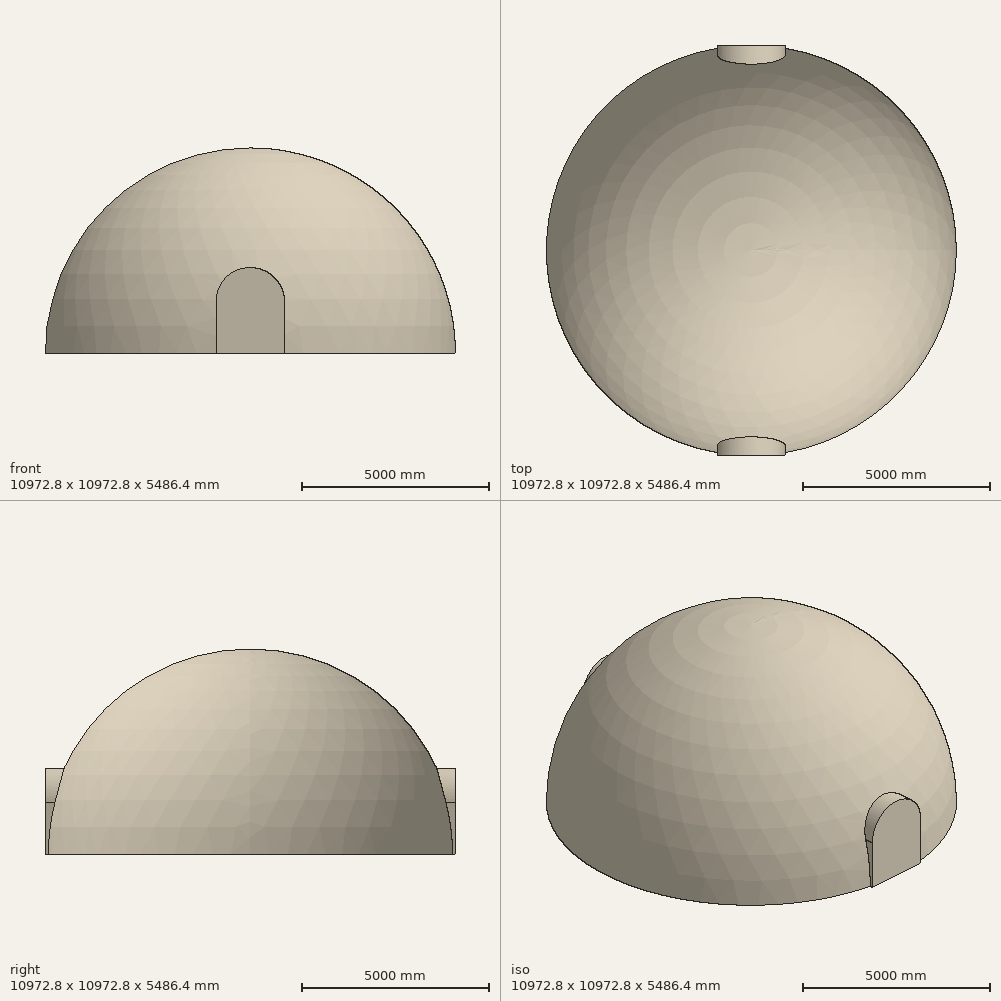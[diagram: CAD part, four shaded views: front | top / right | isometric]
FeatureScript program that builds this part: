
annotation { "Feature Type Name" : "Feature", "Feature Type Description" : "" }
export const myFeature = defineFeature(function(context is Context, id is Id, definition is map)
    precondition{}
    {
        {
            var Q0;
            Q0=qCreatedBy(makeId("Front.planeOp"),FACE);
            var sketch = newSketch(context, id + "F0", { "sketchPlane" : qUnion([Q0])});
            skLineSegment(sketch, "E0", {"start": v(0, 0) * mm, "end": v(5486.4, 0) * mm});
            skLineSegment(sketch, "E1", {"start": v(0, 0) * mm, "end": v(0, 5486.4) * mm, "construction": true});
            skArc(sketch, "E2", {"start": v(0, 5486.4) * mm, "mid": v(3879.47, 3879.47) * mm, "end": v(5486.4, 0) * mm});
            skLineSegment(sketch, "E3", {"start": v(0, 5486.4) * mm, "end": v(0, 0) * mm});
            skSolve(sketch);
        }
        {
            var Q0;
            Q0=makeQuery(id+"F0.imprint","IMPRINT",FACE,{"disambiguationData":[TD([[makeQuery(id+"F0.imprint","IMPRINT",EDGE,{"derivedFrom":sQuery(id+"F0.wireOp",EDGE,"E0")}),1.0]])]});
            var Q1;
            Q1=sQuery(id+"F0.wireOp",EDGE,"E3");
            revolve(context, id + "F1", {"entities" : qUnion([Q0]), "axis" : qUnion([Q1]), "revolveType" : RevolveType.FULL});
        }
        {
            var Q0;
            Q0=qCreatedBy(makeId("Front.planeOp"),FACE);
            var sketch = newSketch(context, id + "F2", { "sketchPlane" : qUnion([Q0])});
            skLineSegment(sketch, "E4", {"start": v(0, 0) * mm, "end": v(914.4, 0) * mm});
            skLineSegment(sketch, "E5", {"start": v(0, 0) * mm, "end": v(-914.4, 0) * mm});
            skLineSegment(sketch, "E6", {"start": v(914.4, 0) * mm, "end": v(914.4, 1371.6) * mm});
            skLineSegment(sketch, "E7", {"start": v(-914.4, 0) * mm, "end": v(-914.4, 1371.6) * mm});
            skArc(sketch, "E8", {"start": v(914.4, 1371.6) * mm, "mid": v(0, 2286) * mm, "end": v(-914.4, 1371.6) * mm});
            skSolve(sketch);
        }
        {
            var Q0;
            Q0 = qSketchRegion(id + "F2", true);
            extrude(context, id + "F3", {"entities" : qUnion([Q0]), "operationType" : NewBodyOperationType.ADD, "depth" : 5486.4 * mm, "hasSecondDirection" : true, "secondDirectionOppositeDirection" : true, "secondDirectionDepth" : 5486.4 * mm});
        }
    });
